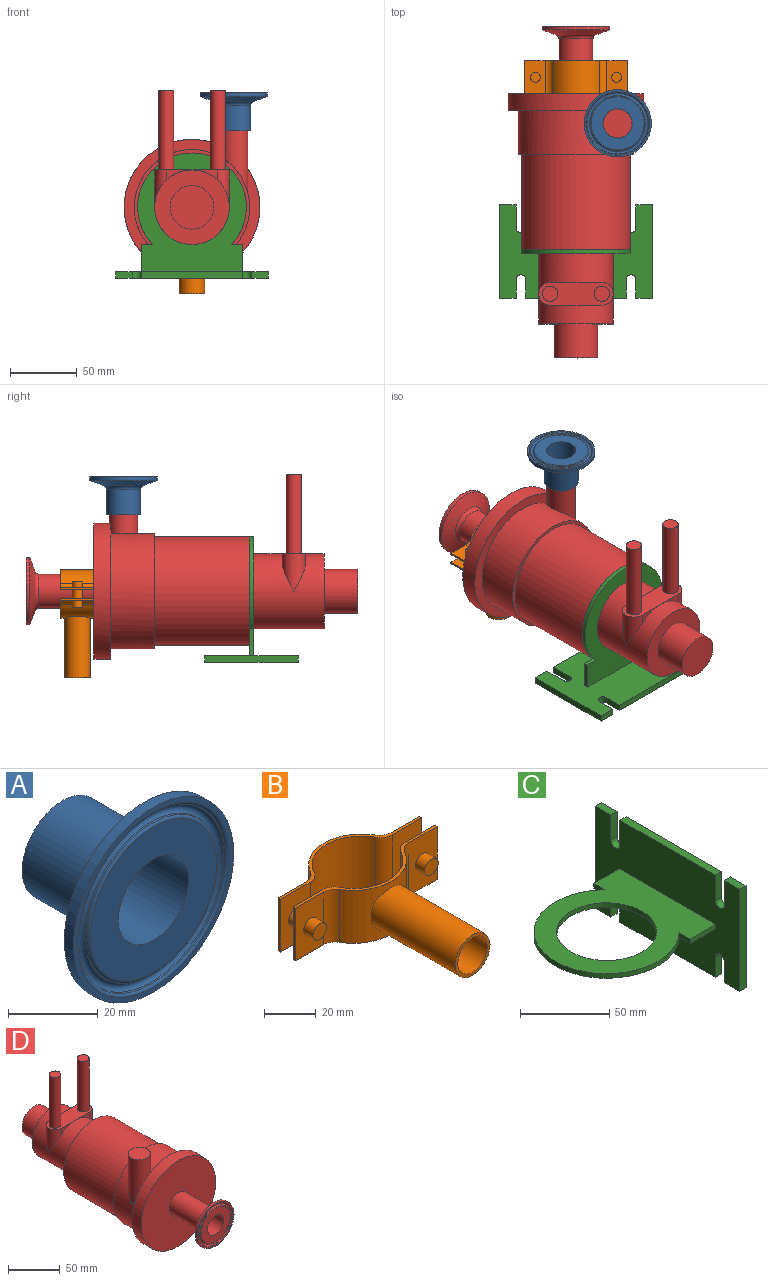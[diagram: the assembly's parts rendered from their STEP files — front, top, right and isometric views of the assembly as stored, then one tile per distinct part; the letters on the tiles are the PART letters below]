
ASSEMBLY  parts=4 mates=3
PART A: 13 faces, bbox 51.5x28.6x51.5 mm
  f0: cylinder r=25.2mm len=50.39mm, axis (0,-1,0), area 450.4mm2, adj f1,f10
  f1: cone r=14.79mm half-angle=70deg, axis (0,-1,0), area 1391.3mm2, adj f0,f2
  f2: torus R=15.88mm, axis (0,-1,0), area 327.4mm2, adj f1,f3
  f3: cylinder r=12.7mm len=25.4mm, axis (0,-1,0), area 1512.8mm2, adj f2,f12
  f4: cylinder r=11.05mm len=28.58mm, axis (0,-1,0), area 1983.8mm2, adj f11,f12
  f5: torus R=19.83mm, axis (0,-1,0), area 117.1mm2, adj f6,f11
  f6: cone r=20.72mm half-angle=23deg, axis (0,1,0), area 55.4mm2, adj f5,f7
  f7: torus R=21.82mm, axis (0,-1,0), area 382.8mm2, adj f6,f8
  f8: cone r=23.08mm half-angle=23deg, axis (0,-1,0), area 61.7mm2, adj f7,f9
  f9: torus R=23.81mm, axis (0,-1,0), area 135.4mm2, adj f8,f10
  f10: plane 50.39x50.39mm, normal (0,-1,0), area 213.6mm2, adj f0,f9
  f11: plane 39.66x39.66mm, normal (0,-1,0), area 851.6mm2, adj f4,f5
  f12: plane 25.4x25.4mm, normal (0,1,0), area 123.2mm2, adj f3,f4
PART B: 43 faces, bbox 76.9x80.7x24.9 mm
  f0: cylinder r=9.53mm len=45.72mm, axis (0,1,0), area 2708.8mm2, adj f1,f2,f4,f5
  f1: plane 12.44x2.31mm, normal (0,1,0), area 15.6mm2, adj f0,f3,f5
  f2: plane 12.44x2.31mm, normal (0,1,0), area 15.6mm2, adj f0,f3,f5
  f3: cylinder r=8.05mm len=45.72mm, axis (0,1,0), area 2284.4mm2, adj f1,f2,f4,f5
  f4: plane 19.05x19.05mm, normal (0,-1,0), area 81.3mm2, adj f0,f3
  f5: cylinder r=20.37mm len=35.28mm, axis (0,0,-1), area 1010.6mm2, adj f0,f1,f2,f3,f11,f12,f17,f18
  f6: cylinder r=19.05mm len=33.55mm, axis (0,0,-1), area 1021.3mm2, adj f7,f16,f17,f18
  f7: cylinder r=6.35mm len=24.89mm, axis (0,0,-1), area 170.2mm2, adj f6,f8,f17,f18
  f8: plane 24.89x16.1mm, normal (0,1,0), area 358.1mm2, adj f7,f9,f17,f18,f38
  f9: plane 24.89x1.32mm, normal (-1,0,0), area 32.9mm2, adj f8,f10,f17,f18
  f10: plane 24.89x15.32mm, normal (0,-1,0), area 338.8mm2, adj f9,f11,f17,f18,f42
  f11: cylinder r=6.35mm len=24.89mm, axis (0,0,-1), area 165.5mm2, adj f5,f10,f17,f18
  f12: cylinder r=6.35mm len=24.89mm, axis (0,0,-1), area 165.5mm2, adj f5,f13,f17,f18
  f13: plane 24.89x15.32mm, normal (0,-1,0), area 338.8mm2, adj f12,f14,f17,f18,f40
  f14: plane 24.89x1.32mm, normal (1,0,0), area 32.9mm2, adj f13,f15,f17,f18
  f15: plane 24.89x16.1mm, normal (0,1,0), area 358.1mm2, adj f14,f16,f17,f18,f19
  f16: cylinder r=6.35mm len=24.89mm, axis (0,0,-1), area 170.2mm2, adj f6,f15,f17,f18
  f17: plane 76.92x14.68mm, normal (0,0,1), area 116.5mm2, adj f5,f6,f7,f8,f9,f10,f11,f12
  f18: plane 76.92x14.68mm, normal (0,0,-1), area 116.5mm2, adj f5,f6,f7,f8,f9,f10,f11,f12
  f19: cylinder r=3.68mm len=7.37mm, axis (0,-1,0), area 161.6mm2, adj f15,f36
  f20: cylinder r=3.68mm len=7.37mm, axis (0,-1,0), area 101.7mm2, adj f21,f34
  f21: plane 7.37x7.37mm, normal (0,1,0), area 42.6mm2, adj f20
  f22: plane 7.37x7.37mm, normal (0,1,0), area 42.6mm2, adj f23
  f23: cylinder r=3.68mm len=7.37mm, axis (0,-1,0), area 101.7mm2, adj f22,f30
  f24: plane 76.92x14.68mm, normal (0,0,-1), area 116.5mm2, adj f26,f27,f28,f29,f30,f31,f32,f33
  f25: plane 76.92x14.68mm, normal (0,0,1), area 116.5mm2, adj f26,f27,f28,f29,f30,f31,f32,f33
  f26: cylinder r=19.05mm len=33.55mm, axis (0,0,-1), area 1021.3mm2, adj f24,f25,f27,f37
  f27: cylinder r=6.35mm len=24.89mm, axis (0,0,-1), area 170.2mm2, adj f24,f25,f26,f28
  f28: plane 24.89x16.1mm, normal (0,-1,0), area 358.1mm2, adj f24,f25,f27,f29,f38
  f29: plane 24.89x1.32mm, normal (-1,0,0), area 32.9mm2, adj f24,f25,f28,f30
  f30: plane 24.89x15.32mm, normal (0,1,0), area 338.8mm2, adj f23,f24,f25,f29,f31
  f31: cylinder r=6.35mm len=24.89mm, axis (0,0,-1), area 165.5mm2, adj f24,f25,f30,f32
  f32: cylinder r=20.37mm len=35.28mm, axis (0,0,-1), area 1062mm2, adj f24,f25,f31,f33
  f33: cylinder r=6.35mm len=24.89mm, axis (0,0,-1), area 165.5mm2, adj f24,f25,f32,f34
  f34: plane 24.89x15.32mm, normal (0,1,0), area 338.8mm2, adj f20,f24,f25,f33,f35
  f35: plane 24.89x1.32mm, normal (1,0,0), area 32.9mm2, adj f24,f25,f34,f36
  f36: plane 24.89x16.1mm, normal (0,-1,0), area 358.1mm2, adj f19,f24,f25,f35,f37
  f37: cylinder r=6.35mm len=24.89mm, axis (0,0,-1), area 170.2mm2, adj f24,f25,f26,f36
  f38: cylinder r=3.68mm len=7.37mm, axis (0,-1,0), area 161.6mm2, adj f8,f28
  f39: plane 7.37x7.37mm, normal (0,-1,0), area 42.6mm2, adj f40
  f40: cylinder r=3.68mm len=7.37mm, axis (0,-1,0), area 116.4mm2, adj f13,f39
  f41: plane 7.37x7.37mm, normal (0,-1,0), area 42.6mm2, adj f42
  f42: cylinder r=3.68mm len=7.37mm, axis (0,-1,0), area 116.4mm2, adj f10,f41
PART C: 30 faces, bbox 93.7x114.3x69.9 mm
  f0: plane 12.32x4.83mm, normal (0,0,1), area 59.5mm2, adj f4,f5,f16,f27
  f1: plane 75.44x4.83mm, normal (0,0,1), area 364.1mm2, adj f4,f5,f20,f29
  f2: plane 12.32x4.83mm, normal (0,0,-1), area 59.5mm2, adj f4,f5,f16,f25
  f3: plane 75.44x4.83mm, normal (0,0,-1), area 364.1mm2, adj f4,f5,f22,f26
  f4: plane 114.3x69.85mm, normal (1,0,0), area 7460mm2, adj f0,f1,f2,f3,f14,f15,f16,f17
  f5: plane 114.3x69.85mm, normal (-1,0,0), area 7218.1mm2, adj f0,f1,f2,f3,f8,f9,f12,f13
  f6: cylinder r=40.64mm len=81.28mm, axis (0,0,-1), area 601mm2, adj f8,f9,f10,f11
  f7: cylinder r=27.94mm len=55.88mm, axis (0,0,-1), area 557.4mm2, adj f8,f9
  f8: plane 88.9x81.28mm, normal (0,0,1), area 3766.8mm2, adj f5,f6,f7,f10,f11,f12,f13
  f9: plane 88.9x81.28mm, normal (0,0,-1), area 3766.8mm2, adj f5,f6,f7,f10,f11,f12,f13
  f10: plane 8.59x3.18mm, normal (-1,0,0), area 27.3mm2, adj f6,f8,f9,f12
  f11: plane 8.59x3.18mm, normal (-1,0,0), area 27.3mm2, adj f6,f8,f9,f13
  f12: plane 20.32x3.18mm, normal (0,-1,0), area 64.5mm2, adj f5,f8,f9,f10
  f13: plane 20.32x3.18mm, normal (0,1,0), area 64.5mm2, adj f5,f8,f9,f11
  f14: plane 69.85x4.83mm, normal (0,1,0), area 337.1mm2, adj f4,f5,f15,f17
  f15: plane 12.32x4.83mm, normal (0,0,1), area 59.5mm2, adj f4,f5,f14,f19
  f16: plane 69.85x4.83mm, normal (0,-1,0), area 337.1mm2, adj f0,f2,f4,f5
  f17: plane 12.32x4.83mm, normal (0,0,-1), area 59.5mm2, adj f4,f5,f14,f23
  f18: cylinder r=3.56mm len=7.11mm, axis (1,0,0), area 53.9mm2, adj f4,f5,f19,f20
  f19: plane 17.21x4.83mm, normal (0,-1,0), area 83mm2, adj f4,f5,f15,f18
  f20: plane 17.21x4.83mm, normal (0,1,0), area 83mm2, adj f1,f4,f5,f18
  f21: cylinder r=3.56mm len=7.11mm, axis (1,0,0), area 53.9mm2, adj f4,f5,f22,f23
  f22: plane 14.03x4.83mm, normal (0,1,0), area 67.7mm2, adj f3,f4,f5,f21
  f23: plane 14.03x4.83mm, normal (0,-1,0), area 67.7mm2, adj f4,f5,f17,f21
  f24: cylinder r=3.56mm len=7.11mm, axis (1,0,0), area 53.9mm2, adj f4,f5,f25,f26
  f25: plane 14.03x4.83mm, normal (0,1,0), area 67.7mm2, adj f2,f4,f5,f24
  f26: plane 14.03x4.83mm, normal (0,-1,0), area 67.7mm2, adj f3,f4,f5,f24
  f27: plane 17.21x4.83mm, normal (0,1,0), area 83mm2, adj f0,f4,f5,f28
  f28: cylinder r=3.56mm len=7.11mm, axis (1,0,0), area 53.9mm2, adj f4,f5,f27,f29
  f29: plane 17.21x4.83mm, normal (0,-1,0), area 83mm2, adj f1,f4,f5,f28
PART D: 37 faces, bbox 101.6x248.4x138.4 mm
  f0: cylinder r=50.8mm len=101.6mm, axis (0,-1,0), area 4042.6mm2, adj f1,f15,f24
  f1: plane 101.6x101.6mm, normal (0,1,0), area 2144.8mm2, adj f0,f2,f24
  f2: cylinder r=43.18mm len=86.36mm, axis (0,-1,0), area 8254.5mm2, adj f1,f16,f24
  f3: cylinder r=25.2mm len=50.39mm, axis (0,-1,0), area 450.4mm2, adj f4,f13
  f4: cone r=14.79mm half-angle=70deg, axis (0,-1,0), area 1391.3mm2, adj f3,f5
  f5: torus R=15.88mm, axis (0,-1,0), area 327.4mm2, adj f4,f6
  f6: cylinder r=12.7mm len=41.18mm, axis (0,-1,0), area 3286.3mm2, adj f5,f15
  f7: cylinder r=11.05mm len=167.13mm, axis (0,-1,0), area 11602.8mm2, adj f14,f21
  f8: torus R=19.83mm, axis (0,-1,0), area 117.1mm2, adj f9,f14
  f9: cone r=20.72mm half-angle=23deg, axis (0,1,0), area 55.4mm2, adj f8,f10
  f10: torus R=21.82mm, axis (0,-1,0), area 382.8mm2, adj f9,f11
  f11: cone r=23.08mm half-angle=23deg, axis (0,-1,0), area 61.7mm2, adj f10,f12
  f12: torus R=23.81mm, axis (0,-1,0), area 135.4mm2, adj f11,f13
  f13: plane 50.39x50.39mm, normal (0,-1,0), area 213.6mm2, adj f3,f12
  f14: plane 39.66x39.66mm, normal (0,-1,0), area 851.6mm2, adj f7,f8
  f15: plane 101.6x101.6mm, normal (0,-1,0), area 7600.6mm2, adj f0,f6
  f16: plane 86.36x86.36mm, normal (0,1,0), area 668.9mm2, adj f2,f17
  f17: cylinder r=40.64mm len=81.28mm, axis (0,-1,0), area 18160.4mm2, adj f16,f18
  f18: plane 81.28x81.28mm, normal (0,1,0), area 2736.2mm2, adj f17,f20
  f19: plane 55.88x55.88mm, normal (0,1,0), area 1609.3mm2, adj f20,f22
  f20: cylinder r=27.94mm len=55.88mm, axis (0,-1,0), area 8596.1mm2, adj f18,f19,f26,f27,f28,f29,f31,f32
  f21: plane 22.1x22.1mm, normal (0,-1,0), area 383.5mm2, adj f7
  f22: cylinder r=16.38mm len=32.77mm, axis (0,-1,0), area 2614.6mm2, adj f19,f23
  f23: plane 32.77x32.77mm, normal (0,1,0), area 843.2mm2, adj f22
  f24: cylinder r=10.73mm len=53.11mm, axis (0,0,-1), area 2329.4mm2, adj f0,f1,f2,f25
  f25: plane 21.46x21.46mm, normal (0,0,1), area 361.8mm2, adj f24
  f26: cylinder r=8.61mm len=27.94mm, axis (0,0,-1), area 456mm2, adj f20,f27,f29,f30
  f27: plane 19.33x7.77mm, normal (0,1,0), area 46.9mm2, adj f20,f26,f30
  f28: cylinder r=8.61mm len=27.94mm, axis (0,0,-1), area 456mm2, adj f20,f30,f31,f32
  f29: plane 19.33x7.77mm, normal (0,-1,0), area 46.9mm2, adj f20,f26,f30
  f30: plane 55.88x17.22mm, normal (0,0,1), area 693.5mm2, adj f26,f27,f28,f29,f31,f32,f33,f35
  f31: plane 19.33x7.77mm, normal (0,1,0), area 46.9mm2, adj f20,f28,f30
  f32: plane 19.33x7.77mm, normal (0,-1,0), area 46.9mm2, adj f20,f28,f30
  f33: cylinder r=5.71mm len=59.69mm, axis (0,0,-1), area 2143.4mm2, adj f30,f34
  f34: plane 11.43x11.43mm, normal (0,0,1), area 102.6mm2, adj f33
  f35: cylinder r=5.71mm len=59.69mm, axis (0,0,-1), area 2143.4mm2, adj f30,f36
  f36: plane 11.43x11.43mm, normal (0,0,1), area 102.6mm2, adj f35
PLACE A rot(axis=(-1,0,0),90deg) t=(241.86,172.56,126.41)mm
PLACE B rot(axis=(1,0,0),90deg) t=(210.68,207.17,21.64)mm
PLACE C rot(axis=(-0.58,0.58,0.58),120deg) t=(210.68,75.21,40.69)mm
PLACE D rot(axis=(0,0,1),180deg) t=(210.68,245.52,40.69)mm
MATE fastened D.f0 <-> B.f6  axis (0,1,0) through (210.68,194.72,40.69)mm
MATE fastened D.f24 <-> A.f0  axis (0,0,1) through (241.86,172.56,104.19)mm
MATE fastened D.f20 <-> C.f7  axis (0,-1,0) through (210.68,78.39,40.69)mm
